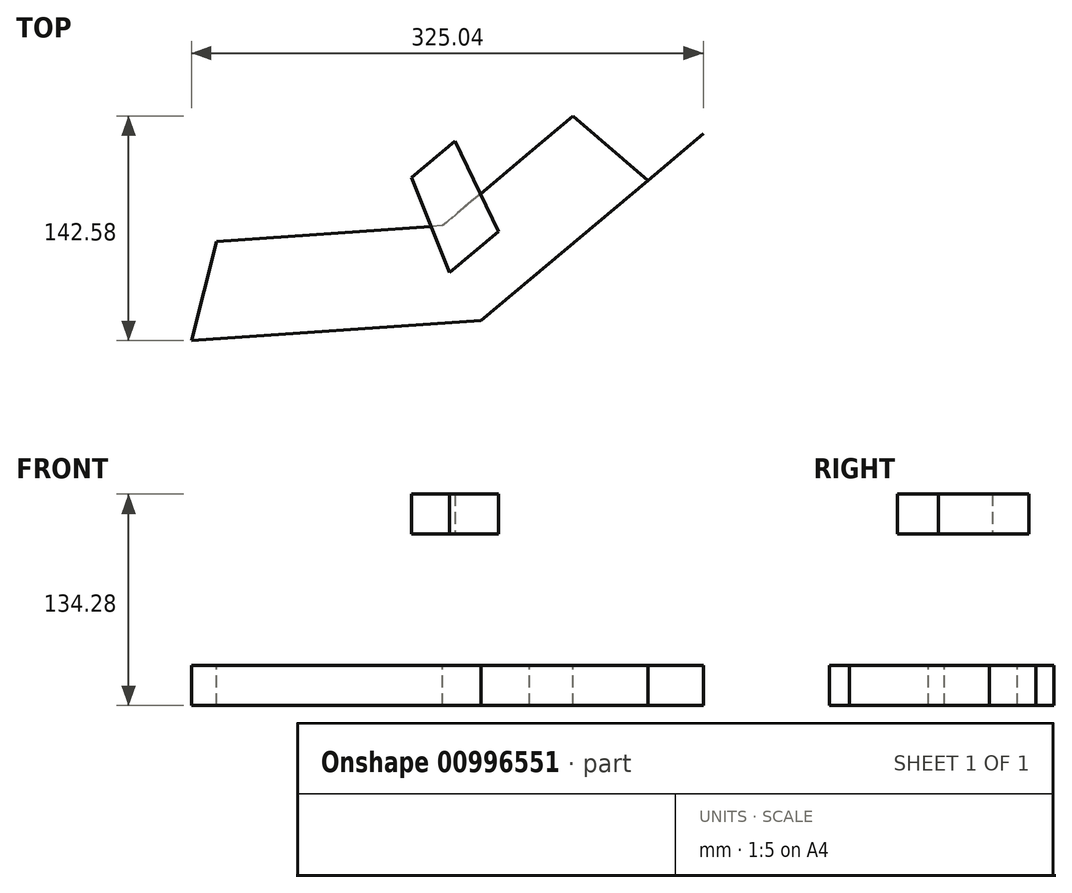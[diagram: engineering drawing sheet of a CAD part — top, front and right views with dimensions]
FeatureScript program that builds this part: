
annotation { "Feature Type Name" : "Feature", "Feature Type Description" : "" }
export const myFeature = defineFeature(function(context is Context, id is Id, definition is map)
    precondition{}
    {
        {
            var Q0;
            Q0=qCreatedBy(makeId("Top.planeOp"),FACE);
            var sketch = newSketch(context, id + "F0", { "sketchPlane" : qUnion([Q0])});
            skLineSegment(sketch, "E0.0", {"start": v(-192.1, 110.91) * mm, "end": v(192.1, 110.91) * mm});
            skLineSegment(sketch, "E0.1", {"start": v(192.1, 110.91) * mm, "end": v(96.05, -55.46) * mm});
            skLineSegment(sketch, "E0.2", {"start": v(0, -221.83) * mm, "end": v(-142.59, 25.14) * mm});
            skPoint(sketch, "E0.0.midPoint", {"position": v(0, 110.91) * mm});
            skLineSegment(sketch, "E1.1.0", {"start": v(142.59, -169.93) * mm, "end": v(-218.46, -38.52) * mm});
            skLineSegment(sketch, "E1.2.0", {"start": v(218.46, -38.52) * mm, "end": v(125.39, -72.4) * mm});
            skPoint(sketch, "E1.center", {"position": v(0, 0) * mm});
            skLineSegment(sketch, "E2.1.1", {"start": v(-218.46, -38.52) * mm, "end": v(75.87, 208.45) * mm});
            skLineSegment(sketch, "E2.1.2", {"start": v(142.59, -169.93) * mm, "end": v(-125.39, -72.4) * mm});
            skLineSegment(sketch, "E2.2.1", {"start": v(-142.59, -169.93) * mm, "end": v(-75.87, 208.45) * mm});
            skLineSegment(sketch, "E3.2.3.0", {"start": v(75.87, 208.45) * mm, "end": v(142.59, -169.93) * mm});
            skLineSegment(sketch, "E3.3.3.0", {"start": v(0, -221.83) * mm, "end": v(-192.1, 110.91) * mm});
            skLineSegment(sketch, "E3.2.4.0", {"start": v(-75.87, 208.45) * mm, "end": v(218.46, -38.52) * mm});
            skLineSegment(sketch, "E3.3.4.0", {"start": v(142.59, -169.93) * mm, "end": v(96.05, -153) * mm});
            skLineSegment(sketch, "E3.6.4.0", {"start": v(75.87, 208.45) * mm, "end": v(142.59, -169.93) * mm});
            skLineSegment(sketch, "E3.6.5.0", {"start": v(-75.87, 208.45) * mm, "end": v(218.46, -38.52) * mm});
            skLineSegment(sketch, "E3.2.6.0", {"start": v(-218.46, -38.52) * mm, "end": v(-217.79, -37.96) * mm});
            skLineSegment(sketch, "E3.2.7.0", {"start": v(-142.59, -169.93) * mm, "end": v(-125.39, -72.4) * mm});
            skLineSegment(sketch, "E3.3.7.0", {"start": v(75.87, 208.45) * mm, "end": v(142.59, -169.93) * mm});
            skLineSegment(sketch, "E3.2.8.0", {"start": v(0, -221.83) * mm, "end": v(-192.1, 110.91) * mm});
            skLineSegment(sketch, "E3.3.8.0", {"start": v(-75.87, 208.45) * mm, "end": v(218.46, -38.52) * mm});
            skLineSegment(sketch, "E4.2.6.0", {"start": v(-192.1, 110.91) * mm, "end": v(-93.07, 110.91) * mm});
            skLineSegment(sketch, "E5", {"start": v(0, -118.03) * mm, "end": v(0, 144.79) * mm});
            skLineSegment(sketch, "E6.1.0", {"start": v(-75.87, -90.42) * mm, "end": v(93.07, 110.91) * mm});
            skLineSegment(sketch, "E6.2.0", {"start": v(-116.24, -20.5) * mm, "end": v(142.59, 25.14) * mm});
            skLineSegment(sketch, "E6.3.0", {"start": v(-102.22, 59.02) * mm, "end": v(125.39, -72.4) * mm});
            skLineSegment(sketch, "E6.4.0", {"start": v(-40.37, 110.91) * mm, "end": v(49.52, -136.05) * mm});
            skLineSegment(sketch, "E6.5.0", {"start": v(40.37, 110.91) * mm, "end": v(-49.52, -136.05) * mm});
            skLineSegment(sketch, "E6.6.0", {"start": v(102.22, 59.02) * mm, "end": v(-125.39, -72.4) * mm});
            skLineSegment(sketch, "E6.7.0", {"start": v(116.24, -20.5) * mm, "end": v(-142.59, 25.14) * mm});
            skLineSegment(sketch, "E6.8.0", {"start": v(0, 0) * mm, "end": v(-93.07, 110.91) * mm});
            skLineSegment(sketch, "E6.anchor1", {"start": v(0, 0) * mm, "end": v(0, -118.03) * mm, "construction": true});
            skLineSegment(sketch, "E7", {"start": v(0, -221.83) * mm, "end": v(-49.52, -136.05) * mm});
            skLineSegment(sketch, "E8", {"start": v(-49.52, -136.05) * mm, "end": v(-142.59, -169.93) * mm});
            skLineSegment(sketch, "E9", {"start": v(-142.6, -170.03) * mm, "end": v(-142.59, -169.93) * mm});
            skLineSegment(sketch, "E10", {"start": v(-125.39, -72.4) * mm, "end": v(-218.46, -38.52) * mm});
            skLineSegment(sketch, "E11", {"start": v(-218.46, -38.52) * mm, "end": v(-142.59, 25.14) * mm});
            skLineSegment(sketch, "E12", {"start": v(-75.87, 208.45) * mm, "end": v(-93.07, 110.91) * mm});
            skLineSegment(sketch, "E13", {"start": v(-75.87, 208.45) * mm, "end": v(0, 144.79) * mm});
            skLineSegment(sketch, "E14", {"start": v(0, 144.79) * mm, "end": v(75.87, 208.45) * mm});
            skLineSegment(sketch, "E15", {"start": v(75.87, 208.45) * mm, "end": v(93.07, 110.91) * mm});
            skLineSegment(sketch, "E16", {"start": v(93.07, 110.91) * mm, "end": v(192.1, 110.91) * mm});
            skLineSegment(sketch, "E17", {"start": v(192.1, 110.91) * mm, "end": v(142.59, 25.14) * mm});
            skLineSegment(sketch, "E18", {"start": v(-142.6, -170.03) * mm, "end": v(-125.39, -72.4) * mm});
            skLineSegment(sketch, "E19", {"start": v(-125.39, -72.4) * mm, "end": v(-75.87, 208.45) * mm});
            skLineSegment(sketch, "E20", {"start": v(-93.07, 110.91) * mm, "end": v(192.1, 110.91) * mm});
            skLineSegment(sketch, "E21", {"start": v(-125.2, -72.46) * mm, "end": v(-125.39, -72.4) * mm});
            skLineSegment(sketch, "E22", {"start": v(-218.46, -38.52) * mm, "end": v(-218.46, -38.52) * mm});
            skLineSegment(sketch, "E23", {"start": v(-217.79, -37.96) * mm, "end": v(75.87, 208.45) * mm});
            skLineSegment(sketch, "E24", {"start": v(-142.59, 25.14) * mm, "end": v(-192.1, 110.91) * mm});
            skLineSegment(sketch, "E25", {"start": v(-142.59, 25.14) * mm, "end": v(-142.59, 25.14) * mm});
            skLineSegment(sketch, "E26.0", {"start": v(197.8, -123.6) * mm, "end": v(87.37, -216.26) * mm});
            skLineSegment(sketch, "E26.1", {"start": v(87.37, -216.26) * mm, "end": v(-56.43, -226.31) * mm});
            skLineSegment(sketch, "E26.2", {"start": v(-56.43, -226.31) * mm, "end": v(-178.67, -149.92) * mm});
            skLineSegment(sketch, "E26.3", {"start": v(-178.67, -149.92) * mm, "end": v(-232.67, -16.27) * mm});
            skLineSegment(sketch, "E26.4", {"start": v(-232.67, -16.27) * mm, "end": v(-197.8, 123.6) * mm});
            skLineSegment(sketch, "E26.5", {"start": v(-197.8, 123.6) * mm, "end": v(-87.37, 216.26) * mm});
            skLineSegment(sketch, "E26.6", {"start": v(-87.37, 216.26) * mm, "end": v(56.43, 226.31) * mm});
            skLineSegment(sketch, "E26.7", {"start": v(56.43, 226.31) * mm, "end": v(178.67, 149.93) * mm});
            skLineSegment(sketch, "E26.8", {"start": v(178.67, 149.93) * mm, "end": v(232.67, 16.27) * mm});
            skLineSegment(sketch, "E26.9", {"start": v(232.67, 16.27) * mm, "end": v(197.8, -123.6) * mm});
            skPoint(sketch, "E26.0.midPoint", {"position": v(142.59, -169.93) * mm});
            skLineSegment(sketch, "E27.0", {"start": v(-252.9, 158.02) * mm, "end": v(-111.7, 276.49) * mm});
            skLineSegment(sketch, "E27.1", {"start": v(-297.48, -20.8) * mm, "end": v(-252.9, 158.02) * mm});
            skLineSegment(sketch, "E27.2", {"start": v(-111.7, 276.49) * mm, "end": v(72.14, 289.35) * mm});
            skLineSegment(sketch, "E27.3", {"start": v(-228.44, -191.68) * mm, "end": v(-297.48, -20.8) * mm});
            skLineSegment(sketch, "E27.4", {"start": v(-72.14, -289.34) * mm, "end": v(-228.44, -191.68) * mm});
            skLineSegment(sketch, "E27.5", {"start": v(111.7, -276.49) * mm, "end": v(-72.14, -289.34) * mm});
            skLineSegment(sketch, "E27.6", {"start": v(72.14, 289.35) * mm, "end": v(228.44, 191.68) * mm});
            skLineSegment(sketch, "E27.7", {"start": v(228.44, 191.68) * mm, "end": v(297.48, 20.8) * mm});
            skLineSegment(sketch, "E27.8", {"start": v(297.48, 20.8) * mm, "end": v(252.9, -158.02) * mm});
            skLineSegment(sketch, "E27.9", {"start": v(252.9, -158.02) * mm, "end": v(111.7, -276.49) * mm});
            skLineSegment(sketch, "E28", {"start": v(-111.7, 276.49) * mm, "end": v(-87.37, 216.26) * mm});
            skLineSegment(sketch, "E29", {"start": v(56.43, 226.31) * mm, "end": v(72.14, 289.35) * mm});
            skLineSegment(sketch, "E30", {"start": v(-297.48, -20.8) * mm, "end": v(-232.67, -16.27) * mm});
            skLineSegment(sketch, "E31", {"start": v(-252.9, 158.02) * mm, "end": v(-192.1, 110.91) * mm});
            skLineSegment(sketch, "E32", {"start": v(228.44, 191.68) * mm, "end": v(178.67, 149.93) * mm});
            skLineSegment(sketch, "E33", {"start": v(111.7, -276.49) * mm, "end": v(87.37, -216.26) * mm});
            skLineSegment(sketch, "E34", {"start": v(-72.14, -289.34) * mm, "end": v(-56.43, -226.31) * mm});
            skLineSegment(sketch, "E35", {"start": v(297.48, 20.8) * mm, "end": v(232.67, 16.27) * mm});
            skLineSegment(sketch, "E36", {"start": v(-228.44, -191.68) * mm, "end": v(-178.67, -149.92) * mm});
            skLineSegment(sketch, "E37", {"start": v(142.59, -169.93) * mm, "end": v(197.8, -123.6) * mm});
            skLineSegment(sketch, "E38", {"start": v(182.3, -217.26) * mm, "end": v(252.9, -158.02) * mm});
            skLineSegment(sketch, "E39", {"start": v(252.9, -158.02) * mm, "end": v(252.9, -158.02) * mm});
            skLineSegment(sketch, "E40", {"start": v(252.9, -158.02) * mm, "end": v(217.6, -187.64) * mm});
            skLineSegment(sketch, "E41", {"start": v(217.6, -187.64) * mm, "end": v(170.2, -146.76) * mm});
            skLineSegment(sketch, "E42", {"start": v(87.37, -216.26) * mm, "end": v(49.52, -136.05) * mm});
            skLineSegment(sketch, "E43", {"start": v(197.8, -123.6) * mm, "end": v(125.39, -72.4) * mm});
            skLineSegment(sketch, "E44", {"start": v(115.12, -192.98) * mm, "end": v(142.59, -250.58) * mm});
            skPoint(sketch, "E45.endSnap0", {"position": v(119.32, -201.79) * mm});
            skPoint(sketch, "E46.endSnap0", {"position": v(91.71, -184.62) * mm});
            skPoint(sketch, "E47.orphan", {"position": v(96.05, -153) * mm});
            skPoint(sketch, "E48.MirrorP", {"position": v(165.9, -122.38) * mm});
            skLineSegment(sketch, "E49.trimOffspring", {"start": v(49.52, -136.05) * mm, "end": v(0, -221.83) * mm});
            skLineSegment(sketch, "E50.trimOffspring", {"start": v(37.93, -104.22) * mm, "end": v(-142.59, -169.93) * mm});
            skLineSegment(sketch, "E51.trimOffspring", {"start": v(85.6, -73.56) * mm, "end": v(85.5, -73.73) * mm});
            skLineSegment(sketch, "E52.trimOffspring", {"start": v(49.52, -136.05) * mm, "end": v(-125.2, -72.46) * mm});
            skPoint(sketch, "E46.end.orphan", {"position": v(72.44, -184.62) * mm});
            skPoint(sketch, "E46.start.orphan", {"position": v(119.32, -161.46) * mm});
            skLineSegment(sketch, "E53.MirrorCS", {"start": v(252.9, -158.02) * mm, "end": v(197.8, -123.6) * mm});
            skLineSegment(sketch, "E54.0", {"start": v(137.5, -141.04) * mm, "end": v(176.36, -108.44) * mm});
            skLineSegment(sketch, "E55.0", {"start": v(176.36, -108.44) * mm, "end": v(137.5, -141.04) * mm});
            skLineSegment(sketch, "E56.trimOffspring", {"start": v(115.03, -159.9) * mm, "end": v(76.16, -192.5) * mm});
            skSolve(sketch);
        }
        {
            var Q0;
            Q0 = qSketchRegion(id + "F0", true);
            var sketch = newSketch(context, id + "F1", { "sketchPlane" : qUnion([Q0])});
            skSolve(sketch);
        }
        {
            var Q0;
            {var subQ1=sQuery(id+"F0.wireOp",EDGE,"E26.5");Q0=makeQuery(id+"F1.imprint","IMPRINT",FACE,{"disambiguationData":[TD([[makeQuery(id+"F1.imprint","IMPRINT",EDGE,{"derivedFrom":makeQuery(id+"F0.imprint","IMPRINT",EDGE,{"derivedFrom":subQ1})}),1.0]])]});}
            var Q1;
            Q1=makeQuery(id+"F1.imprint","IMPRINT",FACE,{"disambiguationData":[TD([[makeQuery(id+"F1.imprint","IMPRINT",EDGE,{"derivedFrom":makeQuery(id+"F0.imprint","IMPRINT",EDGE,{"derivedFrom":sQuery(id+"F0.wireOp",EDGE,"E26.6")})}),1.0]])]});
            var Q2;
            Q2=makeQuery(id+"F0.imprint","IMPRINT",FACE,{"disambiguationData":[TD([[makeQuery(id+"F0.imprint","IMPRINT",EDGE,{"derivedFrom":sQuery(id+"F0.wireOp",EDGE,"E26.1")}),1.0]])]});
            var Q3;
            Q3=makeQuery(id+"F1.imprint","IMPRINT",FACE,{"disambiguationData":[TD([[makeQuery(id+"F1.imprint","IMPRINT",EDGE,{"derivedFrom":makeQuery(id+"F0.imprint","IMPRINT",EDGE,{"derivedFrom":sQuery(id+"F0.wireOp",EDGE,"E27.8")})}),-1.0]])]});
            var Q4;
            {var subQ5=sQuery(id+"F0.wireOp",EDGE,"E38");Q4=makeQuery(id+"F1.imprint","IMPRINT",FACE,{"disambiguationData":[TD([[makeQuery(id+"F1.imprint","IMPRINT",EDGE,{"derivedFrom":makeQuery(id+"F0.imprint","IMPRINT",EDGE,{"derivedFrom":subQ5})}),1.0]])]});}
            var Q5;
            Q5=makeQuery(id+"F1.imprint","IMPRINT",FACE,{"disambiguationData":[TD([[makeQuery(id+"F1.imprint","IMPRINT",EDGE,{"derivedFrom":makeQuery(id+"F0.imprint","IMPRINT",EDGE,{"derivedFrom":sQuery(id+"F0.wireOp",EDGE,"E27.7")})}),-1.0]])]});
            var Q6;
            Q6=makeQuery(id+"F1.imprint","IMPRINT",FACE,{"disambiguationData":[TD([[makeQuery(id+"F1.imprint","IMPRINT",EDGE,{"derivedFrom":makeQuery(id+"F0.imprint","IMPRINT",EDGE,{"derivedFrom":sQuery(id+"F0.wireOp",EDGE,"E26.7")})}),1.0]])]});
            var Q7;
            {var subQ4=sQuery(id+"F0.wireOp",EDGE,"E27.1");Q7=makeQuery(id+"F1.imprint","IMPRINT",FACE,{"disambiguationData":[TD([[makeQuery(id+"F1.imprint","IMPRINT",EDGE,{"derivedFrom":makeQuery(id+"F0.imprint","IMPRINT",EDGE,{"derivedFrom":subQ4})}),-1.0]])]});}
            var Q8;
            Q8=makeQuery(id+"F1.imprint","IMPRINT",FACE,{"disambiguationData":[TD([[makeQuery(id+"F1.imprint","IMPRINT",EDGE,{"derivedFrom":makeQuery(id+"F0.imprint","IMPRINT",EDGE,{"derivedFrom":sQuery(id+"F0.wireOp",EDGE,"E26.2")})}),1.0]])]});
            var Q9;
            {var subQ0=sQuery(id+"F0.wireOp",EDGE,"E33");Q9=makeQuery(id+"F0.imprint","IMPRINT",FACE,{"disambiguationData":[TD([[makeQuery(id+"F0.imprint","IMPRINT",EDGE,{"derivedFrom":subQ0}),-1.0]])]});}
            var Q10;
            Q10=makeQuery(id+"F1.imprint","IMPRINT",FACE,{"disambiguationData":[TD([[makeQuery(id+"F1.imprint","IMPRINT",EDGE,{"derivedFrom":makeQuery(id+"F0.imprint","IMPRINT",EDGE,{"derivedFrom":sQuery(id+"F0.wireOp",EDGE,"E26.3")})}),1.0]])]});
            extrude(context, id + "F2", {"entities" : qUnion([Q0, Q1, Q2, Q3, Q4, Q5, Q6, Q7, Q8, Q9, Q10]), "oppositeDirection" : true, "depth" : 25.4 * mm, "offsetDistance" : 25.4 * mm});
        }
        {
            var Q0;
            Q0=qCreatedBy(makeId("Origin.pointOp"),VERTEX);
            var Q1;
            {var subQ0=sQuery(id+"F0.wireOp",EDGE,"E23");var subQ3=sQuery(id+"F0.wireOp",EDGE,"E6.8.0");var subQ5=makeQuery(id+"F0.imprint","INTERSECT",VERTEX,{"derivedFrom":[subQ3,subQ0]});Q1=makeQuery(id+"F0.imprint","IMPRINT",FACE,{"disambiguationData":[TD([[makeQuery(id+"F0.imprint","IMPRINT",EDGE,{"disambiguationData":[TD([[subQ5,-1.0]])],"derivedFrom":subQ0}),-1.0]])]});}
            cPlane(context, id + "F3", {"entities" : qUnion([Q0, Q1]), "cplaneType" : CPlaneType.PLANE_POINT, "offset" : 25.4 * mm, "width" : 152.4 * mm, "height" : 152.4 * mm});
        }
        {
            var Q0;
            Q0=qCreatedBy(id+"F3.planeOp",FACE);
            cPlane(context, id + "F4", {"entities" : qUnion([Q0]), "cplaneType" : CPlaneType.OFFSET, "offset" : 83.48 * mm, "width" : 152.4 * mm, "height" : 152.4 * mm});
        }
        {
            var Q0;
            Q0=qCreatedBy(id+"F4.planeOp",FACE);
            var sketch = newSketch(context, id + "F5", { "sketchPlane" : qUnion([Q0])});
            skLineSegment(sketch, "E57.0", {"start": v(-212.06, 141.28) * mm, "end": v(172.15, 141.28) * mm});
            skLineSegment(sketch, "E57.1", {"start": v(172.15, 141.28) * mm, "end": v(76.1, -25.1) * mm});
            skLineSegment(sketch, "E57.2", {"start": v(-19.95, -191.46) * mm, "end": v(-162.54, 55.5) * mm});
            skPoint(sketch, "E57.0.midPoint", {"position": v(-19.95, 141.28) * mm});
            skLineSegment(sketch, "E58.1.0", {"start": v(122.63, -139.57) * mm, "end": v(-238.41, -8.16) * mm});
            skLineSegment(sketch, "E58.2.0", {"start": v(198.5, -8.16) * mm, "end": v(105.43, -42.03) * mm});
            skPoint(sketch, "E58.center", {"position": v(-19.95, 30.36) * mm});
            skLineSegment(sketch, "E59.1.1", {"start": v(-238.41, -8.16) * mm, "end": v(55.91, 238.81) * mm});
            skLineSegment(sketch, "E59.1.2", {"start": v(122.63, -139.57) * mm, "end": v(-145.34, -42.03) * mm});
            skLineSegment(sketch, "E59.2.1", {"start": v(-162.54, -139.57) * mm, "end": v(-95.82, 238.81) * mm});
            skLineSegment(sketch, "E60.2.3.0", {"start": v(55.91, 238.81) * mm, "end": v(122.63, -139.57) * mm});
            skLineSegment(sketch, "E60.3.3.0", {"start": v(-19.95, -191.46) * mm, "end": v(-212.06, 141.28) * mm});
            skLineSegment(sketch, "E60.2.4.0", {"start": v(-95.82, 238.81) * mm, "end": v(198.5, -8.16) * mm});
            skLineSegment(sketch, "E60.3.4.0", {"start": v(122.63, -139.57) * mm, "end": v(76.1, -122.63) * mm});
            skLineSegment(sketch, "E60.6.4.0", {"start": v(55.91, 238.81) * mm, "end": v(122.63, -139.57) * mm});
            skLineSegment(sketch, "E60.6.5.0", {"start": v(-95.82, 238.81) * mm, "end": v(198.5, -8.16) * mm});
            skLineSegment(sketch, "E60.2.6.0", {"start": v(-238.41, -8.16) * mm, "end": v(-237.74, -7.6) * mm});
            skLineSegment(sketch, "E60.2.7.0", {"start": v(-162.54, -139.57) * mm, "end": v(-145.34, -42.03) * mm});
            skLineSegment(sketch, "E60.3.7.0", {"start": v(55.91, 238.81) * mm, "end": v(122.63, -139.57) * mm});
            skLineSegment(sketch, "E60.2.8.0", {"start": v(-19.95, -191.46) * mm, "end": v(-212.06, 141.28) * mm});
            skLineSegment(sketch, "E60.3.8.0", {"start": v(-95.82, 238.81) * mm, "end": v(198.5, -8.16) * mm});
            skLineSegment(sketch, "E61.2.6.0", {"start": v(-212.06, 141.28) * mm, "end": v(-113.02, 141.28) * mm});
            skLineSegment(sketch, "E62", {"start": v(-19.95, -87.67) * mm, "end": v(-19.95, 175.15) * mm});
            skLineSegment(sketch, "E63.1.0", {"start": v(-95.82, -60.05) * mm, "end": v(73.11, 141.28) * mm});
            skLineSegment(sketch, "E63.2.0", {"start": v(-136.2, 9.87) * mm, "end": v(122.63, 55.5) * mm});
            skLineSegment(sketch, "E63.3.0", {"start": v(-122.17, 89.38) * mm, "end": v(105.43, -42.03) * mm});
            skLineSegment(sketch, "E63.4.0", {"start": v(-60.32, 141.28) * mm, "end": v(29.57, -105.7) * mm});
            skLineSegment(sketch, "E63.5.0", {"start": v(20.41, 141.28) * mm, "end": v(-69.47, -105.7) * mm});
            skLineSegment(sketch, "E63.6.0", {"start": v(82.26, 89.38) * mm, "end": v(-145.34, -42.03) * mm});
            skLineSegment(sketch, "E63.7.0", {"start": v(96.28, 9.87) * mm, "end": v(-162.54, 55.5) * mm});
            skLineSegment(sketch, "E63.8.0", {"start": v(-19.95, 30.36) * mm, "end": v(-113.02, 141.28) * mm});
            skLineSegment(sketch, "E63.anchor1", {"start": v(-19.95, 30.36) * mm, "end": v(-19.95, -87.67) * mm, "construction": true});
            skLineSegment(sketch, "E64", {"start": v(-19.95, -191.46) * mm, "end": v(-69.47, -105.7) * mm});
            skLineSegment(sketch, "E65", {"start": v(-69.47, -105.7) * mm, "end": v(-162.54, -139.57) * mm});
            skLineSegment(sketch, "E66", {"start": v(-162.56, -139.66) * mm, "end": v(-162.54, -139.57) * mm});
            skLineSegment(sketch, "E67", {"start": v(-145.34, -42.03) * mm, "end": v(-238.41, -8.16) * mm});
            skLineSegment(sketch, "E68", {"start": v(-238.41, -8.16) * mm, "end": v(-162.54, 55.5) * mm});
            skLineSegment(sketch, "E69", {"start": v(-95.82, 238.81) * mm, "end": v(-113.02, 141.28) * mm});
            skLineSegment(sketch, "E70", {"start": v(-95.82, 238.81) * mm, "end": v(-19.95, 175.15) * mm});
            skLineSegment(sketch, "E71", {"start": v(-19.95, 175.15) * mm, "end": v(55.91, 238.81) * mm});
            skLineSegment(sketch, "E72", {"start": v(55.91, 238.81) * mm, "end": v(73.11, 141.28) * mm});
            skLineSegment(sketch, "E73", {"start": v(73.11, 141.28) * mm, "end": v(172.15, 141.28) * mm});
            skLineSegment(sketch, "E74", {"start": v(172.15, 141.28) * mm, "end": v(122.63, 55.5) * mm});
            skLineSegment(sketch, "E75", {"start": v(-162.56, -139.66) * mm, "end": v(-145.34, -42.03) * mm});
            skLineSegment(sketch, "E76", {"start": v(-145.34, -42.03) * mm, "end": v(-95.82, 238.81) * mm});
            skLineSegment(sketch, "E77", {"start": v(-113.02, 141.28) * mm, "end": v(172.15, 141.28) * mm});
            skLineSegment(sketch, "E78", {"start": v(-145.16, -42.1) * mm, "end": v(-145.34, -42.03) * mm});
            skLineSegment(sketch, "E79", {"start": v(-238.41, -8.16) * mm, "end": v(-238.41, -8.16) * mm});
            skLineSegment(sketch, "E80", {"start": v(-237.74, -7.6) * mm, "end": v(55.91, 238.81) * mm});
            skLineSegment(sketch, "E81", {"start": v(-162.54, 55.5) * mm, "end": v(-212.06, 141.28) * mm});
            skLineSegment(sketch, "E82", {"start": v(-162.54, 55.5) * mm, "end": v(-162.54, 55.5) * mm});
            skLineSegment(sketch, "E83.0", {"start": v(177.85, -93.24) * mm, "end": v(67.42, -185.9) * mm});
            skLineSegment(sketch, "E83.1", {"start": v(67.42, -185.9) * mm, "end": v(-76.38, -195.95) * mm});
            skLineSegment(sketch, "E83.2", {"start": v(-76.38, -195.95) * mm, "end": v(-198.63, -119.56) * mm});
            skLineSegment(sketch, "E83.3", {"start": v(-198.63, -119.56) * mm, "end": v(-252.63, 14.1) * mm});
            skLineSegment(sketch, "E83.4", {"start": v(-252.63, 14.1) * mm, "end": v(-217.76, 153.96) * mm});
            skLineSegment(sketch, "E83.5", {"start": v(-217.76, 153.96) * mm, "end": v(-107.33, 246.62) * mm});
            skLineSegment(sketch, "E83.6", {"start": v(-107.33, 246.62) * mm, "end": v(36.47, 256.68) * mm});
            skLineSegment(sketch, "E83.7", {"start": v(36.47, 256.68) * mm, "end": v(158.72, 180.29) * mm});
            skLineSegment(sketch, "E83.8", {"start": v(158.72, 180.29) * mm, "end": v(212.72, 46.64) * mm});
            skLineSegment(sketch, "E83.9", {"start": v(212.72, 46.64) * mm, "end": v(177.85, -93.24) * mm});
            skPoint(sketch, "E83.0.midPoint", {"position": v(122.63, -139.57) * mm});
            skLineSegment(sketch, "E84.0", {"start": v(-272.85, 188.39) * mm, "end": v(-131.66, 306.85) * mm});
            skLineSegment(sketch, "E84.1", {"start": v(-317.43, 9.56) * mm, "end": v(-272.85, 188.39) * mm});
            skLineSegment(sketch, "E84.2", {"start": v(-131.66, 306.85) * mm, "end": v(52.19, 319.7) * mm});
            skLineSegment(sketch, "E84.3", {"start": v(-248.4, -161.32) * mm, "end": v(-317.43, 9.56) * mm});
            skLineSegment(sketch, "E84.4", {"start": v(-92.1, -258.98) * mm, "end": v(-248.4, -161.32) * mm});
            skLineSegment(sketch, "E84.5", {"start": v(91.75, -246.13) * mm, "end": v(-92.1, -258.98) * mm});
            skLineSegment(sketch, "E84.6", {"start": v(52.19, 319.7) * mm, "end": v(208.48, 222.05) * mm});
            skLineSegment(sketch, "E84.7", {"start": v(208.48, 222.05) * mm, "end": v(277.52, 51.17) * mm});
            skLineSegment(sketch, "E84.8", {"start": v(277.52, 51.17) * mm, "end": v(232.94, -127.66) * mm});
            skLineSegment(sketch, "E84.9", {"start": v(232.94, -127.66) * mm, "end": v(91.75, -246.13) * mm});
            skLineSegment(sketch, "E85", {"start": v(-131.66, 306.85) * mm, "end": v(-107.33, 246.62) * mm});
            skLineSegment(sketch, "E86", {"start": v(36.47, 256.68) * mm, "end": v(52.19, 319.7) * mm});
            skLineSegment(sketch, "E87", {"start": v(-317.43, 9.56) * mm, "end": v(-252.63, 14.1) * mm});
            skLineSegment(sketch, "E88", {"start": v(-272.85, 188.39) * mm, "end": v(-212.06, 141.28) * mm});
            skLineSegment(sketch, "E89", {"start": v(208.48, 222.05) * mm, "end": v(158.72, 180.29) * mm});
            skLineSegment(sketch, "E90", {"start": v(91.75, -246.13) * mm, "end": v(67.42, -185.9) * mm});
            skLineSegment(sketch, "E91", {"start": v(-92.1, -258.98) * mm, "end": v(-76.38, -195.95) * mm});
            skLineSegment(sketch, "E92", {"start": v(277.52, 51.17) * mm, "end": v(212.72, 46.64) * mm});
            skLineSegment(sketch, "E93", {"start": v(-248.4, -161.32) * mm, "end": v(-198.63, -119.56) * mm});
            skLineSegment(sketch, "E94", {"start": v(122.63, -139.57) * mm, "end": v(177.85, -93.24) * mm});
            skLineSegment(sketch, "E95", {"start": v(162.34, -186.9) * mm, "end": v(232.94, -127.66) * mm});
            skLineSegment(sketch, "E96", {"start": v(232.94, -127.66) * mm, "end": v(232.94, -127.66) * mm});
            skLineSegment(sketch, "E97", {"start": v(232.94, -127.66) * mm, "end": v(197.64, -157.28) * mm});
            skLineSegment(sketch, "E98", {"start": v(197.64, -157.28) * mm, "end": v(150.24, -116.4) * mm});
            skLineSegment(sketch, "E99", {"start": v(67.42, -185.9) * mm, "end": v(29.57, -105.7) * mm});
            skLineSegment(sketch, "E100", {"start": v(177.85, -93.24) * mm, "end": v(105.43, -42.03) * mm});
            skLineSegment(sketch, "E101", {"start": v(95.16, -162.61) * mm, "end": v(122.63, -220.22) * mm});
            skPoint(sketch, "E102.endSnap0", {"position": v(99.37, -171.42) * mm});
            skPoint(sketch, "E103.endSnap0", {"position": v(71.76, -154.26) * mm});
            skPoint(sketch, "E104.orphan", {"position": v(76.1, -122.63) * mm});
            skPoint(sketch, "E105.MirrorP", {"position": v(145.94, -92.02) * mm});
            skLineSegment(sketch, "E106.trimOffspring", {"start": v(29.57, -105.7) * mm, "end": v(-19.95, -191.46) * mm});
            skLineSegment(sketch, "E107.trimOffspring", {"start": v(17.98, -73.86) * mm, "end": v(-162.54, -139.57) * mm});
            skLineSegment(sketch, "E108.trimOffspring", {"start": v(65.65, -43.2) * mm, "end": v(65.55, -43.37) * mm});
            skLineSegment(sketch, "E109.trimOffspring", {"start": v(29.57, -105.7) * mm, "end": v(-145.16, -42.1) * mm});
            skPoint(sketch, "E103.end.orphan", {"position": v(52.49, -154.26) * mm});
            skPoint(sketch, "E103.start.orphan", {"position": v(99.37, -131.1) * mm});
            skLineSegment(sketch, "E110.MirrorCS", {"start": v(232.94, -127.66) * mm, "end": v(177.85, -93.24) * mm});
            skLineSegment(sketch, "E111.0", {"start": v(117.54, -110.68) * mm, "end": v(156.4, -78.07) * mm});
            skLineSegment(sketch, "E112.0", {"start": v(156.4, -78.07) * mm, "end": v(117.54, -110.68) * mm});
            skLineSegment(sketch, "E113.trimOffspring", {"start": v(95.07, -129.53) * mm, "end": v(56.2, -162.14) * mm});
            skLineSegment(sketch, "E114", {"start": v(177.85, -93.24) * mm, "end": v(232.94, -127.66) * mm});
            skLineSegment(sketch, "E115", {"start": v(150.24, -116.4) * mm, "end": v(197.64, -157.28) * mm});
            skLineSegment(sketch, "E116", {"start": v(197.64, -157.28) * mm, "end": v(197.64, -157.28) * mm});
            skSolve(sketch);
        }
        {
            var Q0;
            {var subQ0=sQuery(id+"F5.wireOp",EDGE,"E90");Q0=makeQuery(id+"F5.imprint","IMPRINT",FACE,{"disambiguationData":[TD([[makeQuery(id+"F5.imprint","IMPRINT",EDGE,{"derivedFrom":subQ0}),-1.0]])]});}
            extrude(context, id + "F6", {"entities" : qUnion([Q0]), "depth" : 25.4 * mm, "offsetDistance" : 25.4 * mm});
        }
    });
